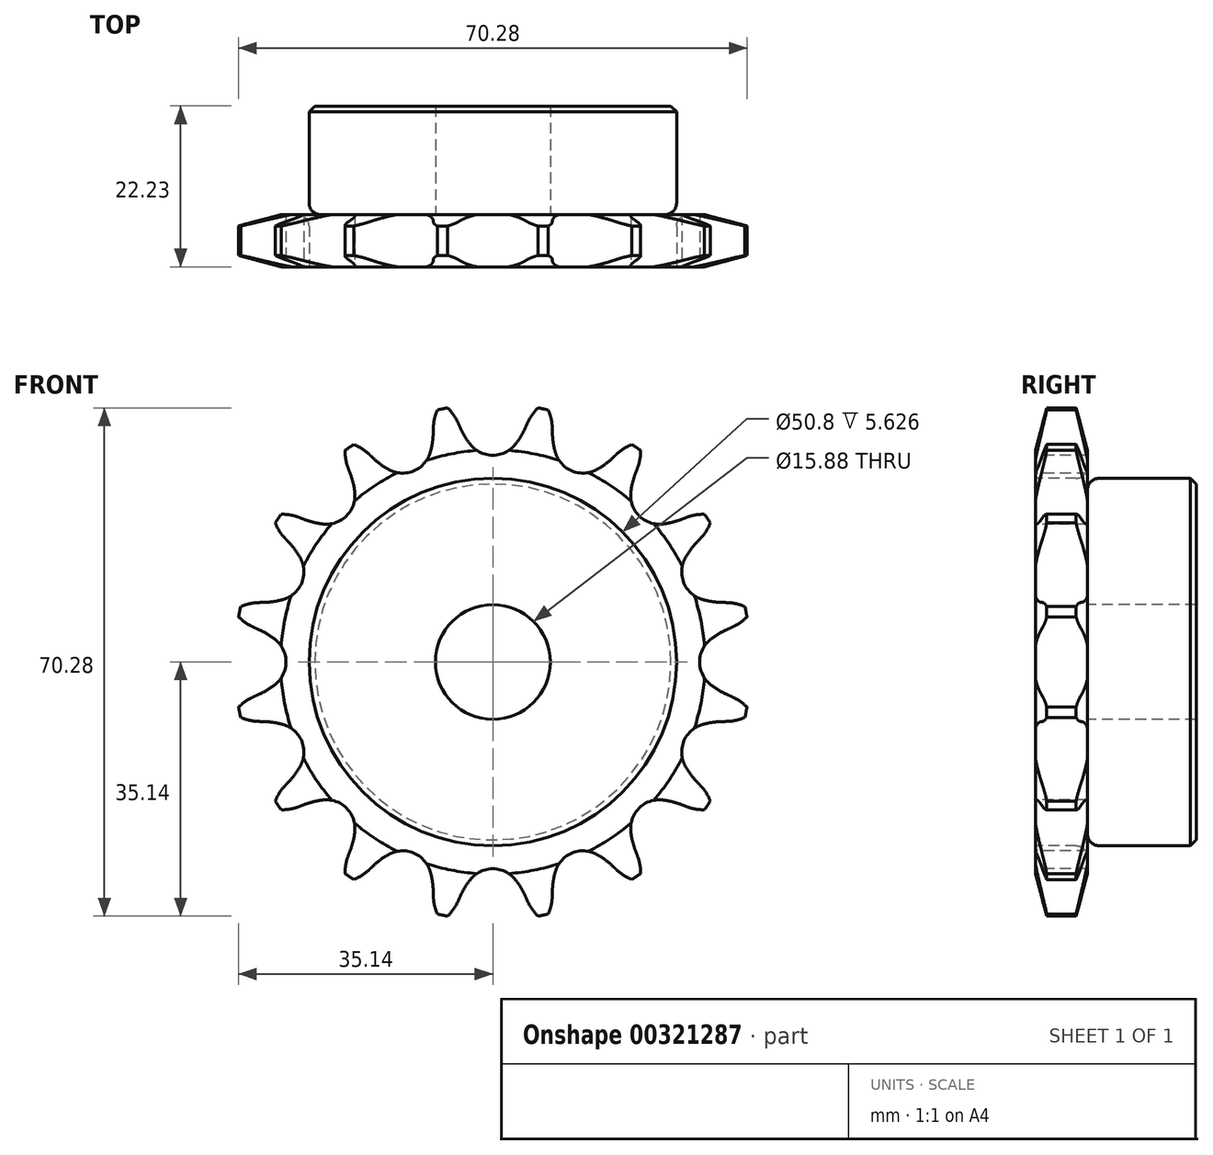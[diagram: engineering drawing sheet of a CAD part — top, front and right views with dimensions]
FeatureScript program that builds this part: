
annotation { "Feature Type Name" : "Feature", "Feature Type Description" : "" }
export const myFeature = defineFeature(function(context is Context, id is Id, definition is map)
    precondition{}
    {
        {
            var Q0;
            Q0=qCreatedBy(makeId("Right.planeOp"),FACE);
            var sketch = newSketch(context, id + "F0", { "sketchPlane" : qUnion([Q0])});
            skLineSegment(sketch, "E0", {"start": v(0, 0) * mm, "end": v(22.23, 0) * mm, "construction": true});
            skLineSegment(sketch, "E1.bottom", {"start": v(0, 7.94) * mm, "end": v(7.21, 7.94) * mm});
            skLineSegment(sketch, "E1.top", {"start": v(0, 35.69) * mm, "end": v(7.21, 35.69) * mm});
            skLineSegment(sketch, "E1.left", {"start": v(0, 7.94) * mm, "end": v(0, 35.69) * mm});
            skLineSegment(sketch, "E1.right", {"start": v(7.21, 7.94) * mm, "end": v(7.21, 35.69) * mm});
            skLineSegment(sketch, "E2.bottom", {"start": v(0, 7.94) * mm, "end": v(22.22, 7.94) * mm});
            skLineSegment(sketch, "E2.top", {"start": v(0, 25.4) * mm, "end": v(22.22, 25.4) * mm});
            skLineSegment(sketch, "E2.left", {"start": v(0, 7.94) * mm, "end": v(0, 25.4) * mm});
            skLineSegment(sketch, "E2.right", {"start": v(22.22, 7.94) * mm, "end": v(22.22, 25.4) * mm});
            skLineSegment(sketch, "E3.MirrorCS", {"start": v(0, -7.94) * mm, "end": v(7.21, -7.94) * mm});
            skLineSegment(sketch, "E4.MirrorCS", {"start": v(22.22, -7.94) * mm, "end": v(22.22, -25.4) * mm});
            skLineSegment(sketch, "E5.MirrorCS", {"start": v(0, -7.94) * mm, "end": v(0, -25.4) * mm});
            skLineSegment(sketch, "E6.MirrorCS", {"start": v(0, -35.69) * mm, "end": v(7.21, -35.69) * mm});
            skLineSegment(sketch, "E7.MirrorCS", {"start": v(0, -7.94) * mm, "end": v(0, -35.69) * mm});
            skLineSegment(sketch, "E8.MirrorCS", {"start": v(7.21, -7.94) * mm, "end": v(7.21, -35.69) * mm});
            skLineSegment(sketch, "E9.MirrorCS", {"start": v(0, -7.94) * mm, "end": v(22.22, -7.94) * mm});
            skLineSegment(sketch, "E10.MirrorCS", {"start": v(0, -25.4) * mm, "end": v(22.22, -25.4) * mm});
            skSolve(sketch);
        }
        {
            var Q0;
            {var subQ5=sQuery(id+"F0.wireOp",EDGE,"E2.left");Q0=makeQuery(id+"F0.imprint","IMPRINT",FACE,{"disambiguationData":[TD([[makeQuery(id+"F0.imprint","IMPRINT",EDGE,{"derivedFrom":subQ5}),-1.0]])]});}
            var Q1;
            {var subQ5=sQuery(id+"F0.wireOp",EDGE,"E2.right");Q1=makeQuery(id+"F0.imprint","IMPRINT",FACE,{"disambiguationData":[TD([[makeQuery(id+"F0.imprint","IMPRINT",EDGE,{"derivedFrom":subQ5}),1.0]])]});}
            var Q2;
            {var subQ0=sQuery(id+"F0.wireOp",EDGE,"E1.top");Q2=makeQuery(id+"F0.imprint","IMPRINT",FACE,{"disambiguationData":[TD([[makeQuery(id+"F0.imprint","IMPRINT",EDGE,{"derivedFrom":subQ0}),-1.0]])]});}
            var Q3;
            Q3=sQuery(id+"F0.wireOp",EDGE,"E0");
            revolve(context, id + "F1", {"entities" : qUnion([Q0, Q1, Q2]), "axis" : qUnion([Q3]), "revolveType" : RevolveType.FULL});
        }
        {
            var Q0;
            Q0=makeQuery(id+"F1.opRevolve","SWEPT_EDGE",EDGE,{"disambiguationData":[OSD([sQuery(id+"F0.wireOp",EDGE,"E2.top"),sQuery(id+"F0.wireOp",EDGE,"E2.right")])]});
            chamfer(context, id + "F2", {"entities" : qUnion([Q0]), "width" : 0.8 * mm, "tangentPropagation" : true});
        }
        {
            var Q0;
            Q0=makeQuery(id+"F1.opRevolve","SWEPT_EDGE",EDGE,{"disambiguationData":[OSD([sQuery(id+"F0.wireOp",EDGE,"E1.right"),sQuery(id+"F0.wireOp",EDGE,"E2.top")])]});
            fillet(context, id + "F3", {"entities" : qUnion([Q0]), "radius" : 1.59 * mm, "tangentPropagation" : true, "allowEdgeOverflow" : false});
        }
        {
            var Q0;
            Q0=makeQuery(id+"F1.opRevolve","SWEPT_FACE",FACE,{"disambiguationData":[OSD([sQuery(id+"F0.wireOp",EDGE,"E1.top")])]});
            chamfer(context, id + "F4", {"entities" : qUnion([Q0]), "chamferType" : ChamferType.TWO_OFFSETS, "width1" : 6.35 * mm, "oppositeDirection" : false, "width2" : 1.57 * mm, "tangentPropagation" : true});
        }
        {
            var Q0;
            Q0=makeQuery(id+"F1.opRevolve","SWEPT_FACE",FACE,{"disambiguationData":[OSD([sQuery(id+"F0.wireOp",EDGE,"E1.left"),sQuery(id+"F0.wireOp",EDGE,"E2.left")])]});
            var sketch = newSketch(context, id + "F5", { "sketchPlane" : qUnion([Q0])});
            skCircle(sketch, "E11", {"center": v(0, 0) * mm, "radius": 32.55 * mm, "construction": true});
            skLineSegment(sketch, "E12", {"start": v(0, 0) * mm, "end": v(0, 32.55) * mm, "construction": true});
            skLineSegment(sketch, "E13", {"start": v(0, 32.55) * mm, "end": v(19.95, 32.55) * mm, "construction": true});
            skLineSegment(sketch, "E14", {"start": v(0, 32.55) * mm, "end": v(5, 36.56) * mm, "construction": true});
            skLineSegment(sketch, "E15", {"start": v(5, 36.56) * mm, "end": v(-4.46, 32.3) * mm, "construction": true});
            skLineSegment(sketch, "E16", {"start": v(-4.46, 32.3) * mm, "end": v(-4.82, 33.1) * mm});
            skLineSegment(sketch, "E17", {"start": v(0, 0) * mm, "end": v(-7.13, 35.85) * mm, "construction": true});
            skArc(sketch, "E18", {"start": v(-7.13, 35.85) * mm, "mid": v(-15.87, 26.15) * mm, "end": v(-4.82, 33.1) * mm, "construction": true});
            skArc(sketch, "E19", {"start": v(-4.82, 33.1) * mm, "mid": v(-5.78, 34.63) * mm, "end": v(-7.13, 35.85) * mm});
            skLineSegment(sketch, "E20", {"start": v(-4.46, 32.3) * mm, "end": v(-4.46, 32.3) * mm});
            skLineSegment(sketch, "E21", {"start": v(-3.1, 30.07) * mm, "end": v(-3.1, 30.07) * mm});
            skArc(sketch, "E22.MirrorCS", {"start": v(4.46, 32.3) * mm, "mid": v(3.84, 31.14) * mm, "end": v(3.1, 30.07) * mm});
            skArc(sketch, "E23.MirrorCS", {"start": v(4.82, 33.1) * mm, "mid": v(5.78, 34.63) * mm, "end": v(7.13, 35.85) * mm});
            skArc(sketch, "E24", {"start": v(-4.46, 32.3) * mm, "mid": v(-3.84, 31.14) * mm, "end": v(-3.1, 30.07) * mm});
            skLineSegment(sketch, "E25", {"start": v(-2.1, 27.05) * mm, "end": v(-4.82, 33.1) * mm, "construction": true});
            skLineSegment(sketch, "E26.MirrorCS", {"start": v(4.46, 32.3) * mm, "end": v(4.82, 33.1) * mm});
            skArc(sketch, "E27", {"start": v(-3.1, 30.07) * mm, "mid": v(13.83, 41.97) * mm, "end": v(-4.46, 32.3) * mm, "construction": true});
            skArc(sketch, "E28", {"start": v(3.1, 30.07) * mm, "mid": v(0, 36.51) * mm, "end": v(-3.1, 30.07) * mm, "construction": true});
            skArc(sketch, "E29", {"start": v(-3.1, 30.07) * mm, "mid": v(0, 28.59) * mm, "end": v(3.1, 30.07) * mm});
            skArc(sketch, "E30.1.0", {"start": v(-17.12, 28.74) * mm, "mid": v(-18.6, 29.79) * mm, "end": v(-20.3, 30.4) * mm});
            skLineSegment(sketch, "E30.1.1", {"start": v(-16.48, 28.14) * mm, "end": v(-17.12, 28.74) * mm});
            skArc(sketch, "E30.1.2", {"start": v(-14.36, 26.6) * mm, "mid": v(-10.94, 26.41) * mm, "end": v(-8.65, 28.96) * mm});
            skArc(sketch, "E30.1.3", {"start": v(-8.22, 32.42) * mm, "mid": v(-7.91, 34.21) * mm, "end": v(-7.13, 35.85) * mm});
            skLineSegment(sketch, "E30.1.4", {"start": v(-8.24, 31.55) * mm, "end": v(-8.22, 32.42) * mm});
            skArc(sketch, "E30.1.5", {"start": v(-8.24, 31.55) * mm, "mid": v(-8.37, 30.24) * mm, "end": v(-8.65, 28.96) * mm});
            skArc(sketch, "E30.1.6", {"start": v(-16.48, 28.14) * mm, "mid": v(-15.47, 27.3) * mm, "end": v(-14.36, 26.6) * mm});
            skArc(sketch, "E30.2.0", {"start": v(-26.8, 20) * mm, "mid": v(-28.58, 20.4) * mm, "end": v(-30.4, 20.3) * mm});
            skLineSegment(sketch, "E30.2.1", {"start": v(-26, 19.69) * mm, "end": v(-26.8, 20) * mm});
            skArc(sketch, "E30.2.2", {"start": v(-23.45, 19.08) * mm, "mid": v(-20.21, 20.21) * mm, "end": v(-19.08, 23.45) * mm});
            skArc(sketch, "E30.2.3", {"start": v(-20, 26.8) * mm, "mid": v(-20.4, 28.58) * mm, "end": v(-20.3, 30.4) * mm});
            skLineSegment(sketch, "E30.2.4", {"start": v(-19.69, 26) * mm, "end": v(-20, 26.8) * mm});
            skArc(sketch, "E30.2.5", {"start": v(-19.69, 26) * mm, "mid": v(-19.3, 24.74) * mm, "end": v(-19.08, 23.45) * mm});
            skArc(sketch, "E30.2.6", {"start": v(-26, 19.69) * mm, "mid": v(-24.74, 19.3) * mm, "end": v(-23.45, 19.08) * mm});
            skArc(sketch, "E31.1.3.0", {"start": v(-32.42, 8.22) * mm, "mid": v(-34.21, 7.91) * mm, "end": v(-35.85, 7.13) * mm});
            skLineSegment(sketch, "E31.4.3.0", {"start": v(-31.55, 8.24) * mm, "end": v(-32.42, 8.22) * mm});
            skArc(sketch, "E31.7.3.0", {"start": v(-28.96, 8.65) * mm, "mid": v(-26.41, 10.94) * mm, "end": v(-26.6, 14.36) * mm});
            skArc(sketch, "E31.11.3.0", {"start": v(-28.74, 17.12) * mm, "mid": v(-29.79, 18.6) * mm, "end": v(-30.4, 20.3) * mm});
            skLineSegment(sketch, "E31.15.3.0", {"start": v(-28.14, 16.48) * mm, "end": v(-28.74, 17.12) * mm});
            skArc(sketch, "E31.18.3.0", {"start": v(-28.14, 16.48) * mm, "mid": v(-27.3, 15.47) * mm, "end": v(-26.6, 14.36) * mm});
            skArc(sketch, "E31.22.3.0", {"start": v(-31.55, 8.24) * mm, "mid": v(-30.24, 8.37) * mm, "end": v(-28.96, 8.65) * mm});
            skArc(sketch, "E31.1.4.0", {"start": v(-33.1, -4.82) * mm, "mid": v(-34.63, -5.78) * mm, "end": v(-35.85, -7.13) * mm});
            skLineSegment(sketch, "E31.4.4.0", {"start": v(-32.3, -4.46) * mm, "end": v(-33.1, -4.82) * mm});
            skArc(sketch, "E31.7.4.0", {"start": v(-30.07, -3.1) * mm, "mid": v(-28.59, 0) * mm, "end": v(-30.07, 3.1) * mm});
            skArc(sketch, "E31.11.4.0", {"start": v(-33.1, 4.82) * mm, "mid": v(-34.63, 5.78) * mm, "end": v(-35.85, 7.13) * mm});
            skLineSegment(sketch, "E31.15.4.0", {"start": v(-32.3, 4.46) * mm, "end": v(-33.1, 4.82) * mm});
            skArc(sketch, "E31.18.4.0", {"start": v(-32.3, 4.46) * mm, "mid": v(-31.14, 3.84) * mm, "end": v(-30.07, 3.1) * mm});
            skArc(sketch, "E31.22.4.0", {"start": v(-32.3, -4.46) * mm, "mid": v(-31.14, -3.84) * mm, "end": v(-30.07, -3.1) * mm});
            skArc(sketch, "E31.1.5.0", {"start": v(-28.74, -17.12) * mm, "mid": v(-29.79, -18.6) * mm, "end": v(-30.4, -20.3) * mm});
            skLineSegment(sketch, "E31.4.5.0", {"start": v(-28.14, -16.48) * mm, "end": v(-28.74, -17.12) * mm});
            skArc(sketch, "E31.7.5.0", {"start": v(-26.6, -14.36) * mm, "mid": v(-26.41, -10.94) * mm, "end": v(-28.96, -8.65) * mm});
            skArc(sketch, "E31.11.5.0", {"start": v(-32.42, -8.22) * mm, "mid": v(-34.21, -7.91) * mm, "end": v(-35.85, -7.13) * mm});
            skLineSegment(sketch, "E31.15.5.0", {"start": v(-31.55, -8.24) * mm, "end": v(-32.42, -8.22) * mm});
            skArc(sketch, "E31.18.5.0", {"start": v(-31.55, -8.24) * mm, "mid": v(-30.24, -8.37) * mm, "end": v(-28.96, -8.65) * mm});
            skArc(sketch, "E31.22.5.0", {"start": v(-28.14, -16.48) * mm, "mid": v(-27.3, -15.47) * mm, "end": v(-26.6, -14.36) * mm});
            skArc(sketch, "E31.1.6.0", {"start": v(-20, -26.8) * mm, "mid": v(-20.4, -28.58) * mm, "end": v(-20.3, -30.4) * mm});
            skLineSegment(sketch, "E31.4.6.0", {"start": v(-19.69, -26) * mm, "end": v(-20, -26.8) * mm});
            skArc(sketch, "E31.7.6.0", {"start": v(-19.08, -23.45) * mm, "mid": v(-20.21, -20.21) * mm, "end": v(-23.45, -19.08) * mm});
            skArc(sketch, "E31.11.6.0", {"start": v(-26.8, -20) * mm, "mid": v(-28.58, -20.4) * mm, "end": v(-30.4, -20.3) * mm});
            skLineSegment(sketch, "E31.15.6.0", {"start": v(-26, -19.69) * mm, "end": v(-26.8, -20) * mm});
            skArc(sketch, "E31.18.6.0", {"start": v(-26, -19.69) * mm, "mid": v(-24.74, -19.3) * mm, "end": v(-23.45, -19.08) * mm});
            skArc(sketch, "E31.22.6.0", {"start": v(-19.69, -26) * mm, "mid": v(-19.3, -24.74) * mm, "end": v(-19.08, -23.45) * mm});
            skArc(sketch, "E31.1.7.0", {"start": v(-8.22, -32.42) * mm, "mid": v(-7.91, -34.21) * mm, "end": v(-7.13, -35.85) * mm});
            skLineSegment(sketch, "E31.4.7.0", {"start": v(-8.24, -31.55) * mm, "end": v(-8.22, -32.42) * mm});
            skArc(sketch, "E31.7.7.0", {"start": v(-8.65, -28.96) * mm, "mid": v(-10.94, -26.41) * mm, "end": v(-14.36, -26.6) * mm});
            skArc(sketch, "E31.11.7.0", {"start": v(-17.12, -28.74) * mm, "mid": v(-18.6, -29.79) * mm, "end": v(-20.3, -30.4) * mm});
            skLineSegment(sketch, "E31.15.7.0", {"start": v(-16.48, -28.14) * mm, "end": v(-17.12, -28.74) * mm});
            skArc(sketch, "E31.18.7.0", {"start": v(-16.48, -28.14) * mm, "mid": v(-15.47, -27.3) * mm, "end": v(-14.36, -26.6) * mm});
            skArc(sketch, "E31.22.7.0", {"start": v(-8.24, -31.55) * mm, "mid": v(-8.37, -30.24) * mm, "end": v(-8.65, -28.96) * mm});
            skArc(sketch, "E31.1.8.0", {"start": v(4.82, -33.1) * mm, "mid": v(5.78, -34.63) * mm, "end": v(7.13, -35.85) * mm});
            skLineSegment(sketch, "E31.4.8.0", {"start": v(4.46, -32.3) * mm, "end": v(4.82, -33.1) * mm});
            skArc(sketch, "E31.7.8.0", {"start": v(3.1, -30.07) * mm, "mid": v(0, -28.59) * mm, "end": v(-3.1, -30.07) * mm});
            skArc(sketch, "E31.11.8.0", {"start": v(-4.82, -33.1) * mm, "mid": v(-5.78, -34.63) * mm, "end": v(-7.13, -35.85) * mm});
            skLineSegment(sketch, "E31.15.8.0", {"start": v(-4.46, -32.3) * mm, "end": v(-4.82, -33.1) * mm});
            skArc(sketch, "E31.18.8.0", {"start": v(-4.46, -32.3) * mm, "mid": v(-3.84, -31.14) * mm, "end": v(-3.1, -30.07) * mm});
            skArc(sketch, "E31.22.8.0", {"start": v(4.46, -32.3) * mm, "mid": v(3.84, -31.14) * mm, "end": v(3.1, -30.07) * mm});
            skArc(sketch, "E31.1.9.0", {"start": v(17.12, -28.74) * mm, "mid": v(18.6, -29.79) * mm, "end": v(20.3, -30.4) * mm});
            skLineSegment(sketch, "E31.4.9.0", {"start": v(16.48, -28.14) * mm, "end": v(17.12, -28.74) * mm});
            skArc(sketch, "E31.7.9.0", {"start": v(14.36, -26.6) * mm, "mid": v(10.94, -26.41) * mm, "end": v(8.65, -28.96) * mm});
            skArc(sketch, "E31.11.9.0", {"start": v(8.22, -32.42) * mm, "mid": v(7.91, -34.21) * mm, "end": v(7.13, -35.85) * mm});
            skLineSegment(sketch, "E31.15.9.0", {"start": v(8.24, -31.55) * mm, "end": v(8.22, -32.42) * mm});
            skArc(sketch, "E31.18.9.0", {"start": v(8.24, -31.55) * mm, "mid": v(8.37, -30.24) * mm, "end": v(8.65, -28.96) * mm});
            skArc(sketch, "E31.22.9.0", {"start": v(16.48, -28.14) * mm, "mid": v(15.47, -27.3) * mm, "end": v(14.36, -26.6) * mm});
            skArc(sketch, "E31.1.10.0", {"start": v(26.8, -20) * mm, "mid": v(28.58, -20.4) * mm, "end": v(30.4, -20.3) * mm});
            skLineSegment(sketch, "E31.4.10.0", {"start": v(26, -19.69) * mm, "end": v(26.8, -20) * mm});
            skArc(sketch, "E31.7.10.0", {"start": v(23.45, -19.08) * mm, "mid": v(20.21, -20.21) * mm, "end": v(19.08, -23.45) * mm});
            skArc(sketch, "E31.11.10.0", {"start": v(20, -26.8) * mm, "mid": v(20.4, -28.58) * mm, "end": v(20.3, -30.4) * mm});
            skLineSegment(sketch, "E31.15.10.0", {"start": v(19.69, -26) * mm, "end": v(20, -26.8) * mm});
            skArc(sketch, "E31.18.10.0", {"start": v(19.69, -26) * mm, "mid": v(19.3, -24.74) * mm, "end": v(19.08, -23.45) * mm});
            skArc(sketch, "E31.22.10.0", {"start": v(26, -19.69) * mm, "mid": v(24.74, -19.3) * mm, "end": v(23.45, -19.08) * mm});
            skArc(sketch, "E31.1.11.0", {"start": v(32.42, -8.22) * mm, "mid": v(34.21, -7.91) * mm, "end": v(35.85, -7.13) * mm});
            skLineSegment(sketch, "E31.4.11.0", {"start": v(31.55, -8.24) * mm, "end": v(32.42, -8.22) * mm});
            skArc(sketch, "E31.7.11.0", {"start": v(28.96, -8.65) * mm, "mid": v(26.41, -10.94) * mm, "end": v(26.6, -14.36) * mm});
            skArc(sketch, "E31.11.11.0", {"start": v(28.74, -17.12) * mm, "mid": v(29.79, -18.6) * mm, "end": v(30.4, -20.3) * mm});
            skLineSegment(sketch, "E31.15.11.0", {"start": v(28.14, -16.48) * mm, "end": v(28.74, -17.12) * mm});
            skArc(sketch, "E31.18.11.0", {"start": v(28.14, -16.48) * mm, "mid": v(27.3, -15.47) * mm, "end": v(26.6, -14.36) * mm});
            skArc(sketch, "E31.22.11.0", {"start": v(31.55, -8.24) * mm, "mid": v(30.24, -8.37) * mm, "end": v(28.96, -8.65) * mm});
            skArc(sketch, "E31.1.12.0", {"start": v(33.1, 4.82) * mm, "mid": v(34.63, 5.78) * mm, "end": v(35.85, 7.13) * mm});
            skLineSegment(sketch, "E31.4.12.0", {"start": v(32.3, 4.46) * mm, "end": v(33.1, 4.82) * mm});
            skArc(sketch, "E31.7.12.0", {"start": v(30.07, 3.1) * mm, "mid": v(28.59, 0) * mm, "end": v(30.07, -3.1) * mm});
            skArc(sketch, "E31.11.12.0", {"start": v(33.1, -4.82) * mm, "mid": v(34.63, -5.78) * mm, "end": v(35.85, -7.13) * mm});
            skLineSegment(sketch, "E31.15.12.0", {"start": v(32.3, -4.46) * mm, "end": v(33.1, -4.82) * mm});
            skArc(sketch, "E31.18.12.0", {"start": v(32.3, -4.46) * mm, "mid": v(31.14, -3.84) * mm, "end": v(30.07, -3.1) * mm});
            skArc(sketch, "E31.22.12.0", {"start": v(32.3, 4.46) * mm, "mid": v(31.14, 3.84) * mm, "end": v(30.07, 3.1) * mm});
            skArc(sketch, "E31.1.13.0", {"start": v(28.74, 17.12) * mm, "mid": v(29.79, 18.6) * mm, "end": v(30.4, 20.3) * mm});
            skLineSegment(sketch, "E31.4.13.0", {"start": v(28.14, 16.48) * mm, "end": v(28.74, 17.12) * mm});
            skArc(sketch, "E31.7.13.0", {"start": v(26.6, 14.36) * mm, "mid": v(26.41, 10.94) * mm, "end": v(28.96, 8.65) * mm});
            skArc(sketch, "E31.11.13.0", {"start": v(32.42, 8.22) * mm, "mid": v(34.21, 7.91) * mm, "end": v(35.85, 7.13) * mm});
            skLineSegment(sketch, "E31.15.13.0", {"start": v(31.55, 8.24) * mm, "end": v(32.42, 8.22) * mm});
            skArc(sketch, "E31.18.13.0", {"start": v(31.55, 8.24) * mm, "mid": v(30.24, 8.37) * mm, "end": v(28.96, 8.65) * mm});
            skArc(sketch, "E31.22.13.0", {"start": v(28.14, 16.48) * mm, "mid": v(27.3, 15.47) * mm, "end": v(26.6, 14.36) * mm});
            skArc(sketch, "E31.1.14.0", {"start": v(20, 26.8) * mm, "mid": v(20.4, 28.58) * mm, "end": v(20.3, 30.4) * mm});
            skLineSegment(sketch, "E31.4.14.0", {"start": v(19.69, 26) * mm, "end": v(20, 26.8) * mm});
            skArc(sketch, "E31.7.14.0", {"start": v(19.08, 23.45) * mm, "mid": v(20.21, 20.21) * mm, "end": v(23.45, 19.08) * mm});
            skArc(sketch, "E31.11.14.0", {"start": v(26.8, 20) * mm, "mid": v(28.58, 20.4) * mm, "end": v(30.4, 20.3) * mm});
            skLineSegment(sketch, "E31.15.14.0", {"start": v(26, 19.69) * mm, "end": v(26.8, 20) * mm});
            skArc(sketch, "E31.18.14.0", {"start": v(26, 19.69) * mm, "mid": v(24.74, 19.3) * mm, "end": v(23.45, 19.08) * mm});
            skArc(sketch, "E31.22.14.0", {"start": v(19.69, 26) * mm, "mid": v(19.3, 24.74) * mm, "end": v(19.08, 23.45) * mm});
            skArc(sketch, "E31.1.15.0", {"start": v(8.22, 32.42) * mm, "mid": v(7.91, 34.21) * mm, "end": v(7.13, 35.85) * mm});
            skLineSegment(sketch, "E31.4.15.0", {"start": v(8.24, 31.55) * mm, "end": v(8.22, 32.42) * mm});
            skArc(sketch, "E31.7.15.0", {"start": v(8.65, 28.96) * mm, "mid": v(10.94, 26.41) * mm, "end": v(14.36, 26.6) * mm});
            skArc(sketch, "E31.11.15.0", {"start": v(17.12, 28.74) * mm, "mid": v(18.6, 29.79) * mm, "end": v(20.3, 30.4) * mm});
            skLineSegment(sketch, "E31.15.15.0", {"start": v(16.48, 28.14) * mm, "end": v(17.12, 28.74) * mm});
            skArc(sketch, "E31.18.15.0", {"start": v(16.48, 28.14) * mm, "mid": v(15.47, 27.3) * mm, "end": v(14.36, 26.6) * mm});
            skArc(sketch, "E31.22.15.0", {"start": v(8.24, 31.55) * mm, "mid": v(8.37, 30.24) * mm, "end": v(8.65, 28.96) * mm});
            skSolve(sketch);
        }
        {
            var Q0;
            Q0 = qSketchRegion(id + "F5", true);
            extrude(context, id + "F6", {"entities" : qUnion([Q0]), "operationType" : NewBodyOperationType.INTERSECT, "endBound" : BoundingType.THROUGH_ALL, "oppositeDirection" : true, "depth" : 25.4 * mm});
        }
    });
